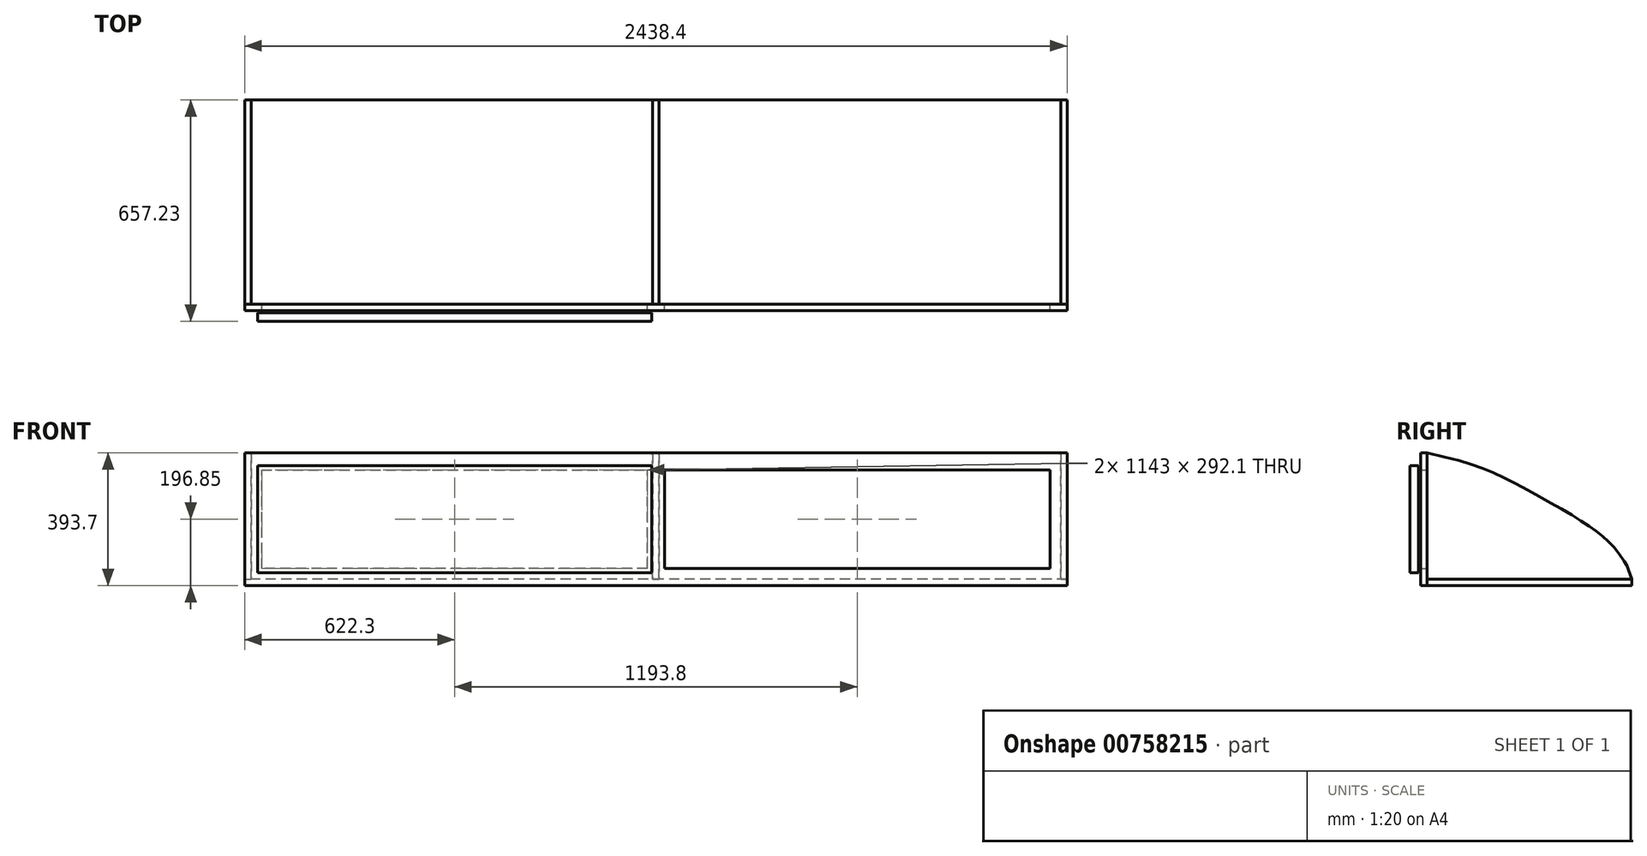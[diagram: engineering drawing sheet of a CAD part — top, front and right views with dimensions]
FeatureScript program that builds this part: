
annotation { "Feature Type Name" : "Feature", "Feature Type Description" : "" }
export const myFeature = defineFeature(function(context is Context, id is Id, definition is map)
    precondition{}
    {
        {
            var Q0;
            Q0=qCreatedBy(makeId("Front.planeOp"),FACE);
            var sketch = newSketch(context, id + "F0", { "sketchPlane" : qUnion([Q0])});
            skLineSegment(sketch, "E0", {"start": v(-1150.95, 0) * mm, "end": v(1287.45, 0) * mm});
            skLineSegment(sketch, "E1", {"start": v(1287.45, 0) * mm, "end": v(1287.45, 50.8) * mm});
            skLineSegment(sketch, "E2", {"start": v(1287.45, 50.8) * mm, "end": v(-1150.95, 50.8) * mm});
            skLineSegment(sketch, "E3", {"start": v(-1150.95, 50.8) * mm, "end": v(-1150.95, 0) * mm});
            skLineSegment(sketch, "E4.bottom", {"start": v(-1150.95, 50.8) * mm, "end": v(-1100.15, 50.8) * mm});
            skLineSegment(sketch, "E4.top", {"start": v(-1150.95, 342.9) * mm, "end": v(-1100.15, 342.9) * mm});
            skLineSegment(sketch, "E4.left", {"start": v(-1150.95, 50.8) * mm, "end": v(-1150.95, 342.9) * mm});
            skLineSegment(sketch, "E4.right", {"start": v(-1100.15, 50.8) * mm, "end": v(-1100.15, 342.9) * mm});
            skLineSegment(sketch, "E5.bottom", {"start": v(1287.45, 50.8) * mm, "end": v(1236.65, 50.8) * mm});
            skLineSegment(sketch, "E5.top", {"start": v(1287.45, 342.9) * mm, "end": v(1236.65, 342.9) * mm});
            skLineSegment(sketch, "E5.left", {"start": v(1287.45, 50.8) * mm, "end": v(1287.45, 342.9) * mm});
            skLineSegment(sketch, "E5.right", {"start": v(1236.65, 50.8) * mm, "end": v(1236.65, 342.9) * mm});
            skLineSegment(sketch, "E6.left", {"start": v(93.65, 50.8) * mm, "end": v(93.65, 342.9) * mm});
            skLineSegment(sketch, "E6.right", {"start": v(42.85, 50.8) * mm, "end": v(42.85, 342.9) * mm});
            skLineSegment(sketch, "E7.bottom", {"start": v(-1150.95, 342.9) * mm, "end": v(1287.45, 342.9) * mm});
            skLineSegment(sketch, "E7.top", {"start": v(-1150.95, 393.7) * mm, "end": v(1287.45, 393.7) * mm});
            skLineSegment(sketch, "E7.left", {"start": v(-1150.95, 342.9) * mm, "end": v(-1150.95, 393.7) * mm});
            skLineSegment(sketch, "E7.right", {"start": v(1287.45, 342.9) * mm, "end": v(1287.45, 393.7) * mm});
            skLineSegment(sketch, "E8", {"start": v(68.25, 342.9) * mm, "end": v(68.25, 50.8) * mm, "construction": true});
            skLineSegment(sketch, "E9", {"start": v(42.85, 342.9) * mm, "end": v(93.65, 342.9) * mm});
            skLineSegment(sketch, "E10", {"start": v(42.85, 50.8) * mm, "end": v(93.65, 50.8) * mm});
            skSolve(sketch);
        }
        {
            var Q0;
            {var subQ1=sQuery(id+"F0.wireOp",EDGE,"E4.top");Q0=makeQuery(id+"F0.imprint","IMPRINT",FACE,{"disambiguationData":[TD([[makeQuery(id+"F0.imprint","IMPRINT",EDGE,{"derivedFrom":subQ1}),1.0]])]});}
            var Q1;
            Q1=makeQuery(id+"F0.imprint","IMPRINT",FACE,{"disambiguationData":[TD([[makeQuery(id+"F0.imprint","IMPRINT",EDGE,{"derivedFrom":sQuery(id+"F0.wireOp",EDGE,"E4.top")}),-1.0]])]});
            var Q2;
            Q2=makeQuery(id+"F0.imprint","IMPRINT",FACE,{"disambiguationData":[TD([[makeQuery(id+"F0.imprint","IMPRINT",EDGE,{"derivedFrom":sQuery(id+"F0.wireOp",EDGE,"E0")}),1.0]])]});
            var Q3;
            {var subQ0=sQuery(id+"F0.wireOp",EDGE,"E6.left");Q3=makeQuery(id+"F0.imprint","IMPRINT",FACE,{"disambiguationData":[TD([[makeQuery(id+"F0.imprint","IMPRINT",EDGE,{"derivedFrom":subQ0}),1.0]])]});}
            var Q4;
            Q4=makeQuery(id+"F0.imprint","IMPRINT",FACE,{"disambiguationData":[TD([[makeQuery(id+"F0.imprint","IMPRINT",EDGE,{"derivedFrom":sQuery(id+"F0.wireOp",EDGE,"E5.top")}),1.0]])]});
            extrude(context, id + "F1", {"entities" : qUnion([Q0, Q1, Q2, Q3, Q4]), "depth" : 19.05 * mm, "offsetDistance" : 25.4 * mm});
        }
        {
            var Q0;
            Q0=makeQuery(id+"F1.opExtrude","CAP_FACE",FACE,{"disambiguationData":[OSD([sQuery(id+"F0.wireOp",EDGE,"E0"),sQuery(id+"F0.wireOp",EDGE,"E1"),sQuery(id+"F0.wireOp",EDGE,"E2"),sQuery(id+"F0.wireOp",EDGE,"E3"),sQuery(id+"F0.wireOp",EDGE,"E4.left"),sQuery(id+"F0.wireOp",EDGE,"E4.right"),sQuery(id+"F0.wireOp",EDGE,"E5.left"),sQuery(id+"F0.wireOp",EDGE,"E5.right"),sQuery(id+"F0.wireOp",EDGE,"E6.left"),sQuery(id+"F0.wireOp",EDGE,"E6.right"),sQuery(id+"F0.wireOp",EDGE,"E7.bottom"),sQuery(id+"F0.wireOp",EDGE,"E7.top"),sQuery(id+"F0.wireOp",EDGE,"E7.left"),sQuery(id+"F0.wireOp",EDGE,"E7.right")])],"isStart":true});
            var sketch = newSketch(context, id + "F2", { "sketchPlane" : qUnion([Q0])});
            skLineSegment(sketch, "E11.bottom", {"start": v(-1287.45, 0) * mm, "end": v(1150.95, 0) * mm});
            skLineSegment(sketch, "E11.top", {"start": v(-1287.45, 19.05) * mm, "end": v(1150.95, 19.05) * mm});
            skLineSegment(sketch, "E11.left", {"start": v(-1287.45, 0) * mm, "end": v(-1287.45, 19.05) * mm});
            skLineSegment(sketch, "E11.right", {"start": v(1150.95, 0) * mm, "end": v(1150.95, 19.05) * mm});
            skSolve(sketch);
        }
        {
            var Q0;
            Q0=makeQuery(id+"F2.imprint","IMPRINT",FACE,{"disambiguationData":[TD([[makeQuery(id+"F2.imprint","IMPRINT",EDGE,{"derivedFrom":sQuery(id+"F2.wireOp",EDGE,"E11.bottom")}),-1.0]])]});
            extrude(context, id + "F3", {"entities" : qUnion([Q0]), "depth" : 606.42 * mm, "offsetDistance" : 25.4 * mm});
        }
        {
            var Q0;
            Q0=makeQuery(id+"F1.opExtrude","SWEPT_FACE",FACE,{"disambiguationData":[OSD([sQuery(id+"F0.wireOp",EDGE,"E1"),sQuery(id+"F0.wireOp",EDGE,"E5.left"),sQuery(id+"F0.wireOp",EDGE,"E7.right")])]});
            cPlane(context, id + "F4", {"entities" : qUnion([Q0]), "cplaneType" : CPlaneType.OFFSET, "offset" : 0 * mm, "width" : 152.4 * mm, "height" : 152.4 * mm});
        }
        {
            var Q0;
            Q0=qCreatedBy(id+"F4.planeOp",FACE);
            var sketch = newSketch(context, id + "F5", { "sketchPlane" : qUnion([Q0])});
            skLineSegment(sketch, "E12.0", {"start": v(0, 19.05) * mm, "end": v(0, 393.7) * mm});
            skLineSegment(sketch, "E13.0", {"start": v(606.43, 19.05) * mm, "end": v(0, 19.05) * mm});
            skLineSegment(sketch, "E14.0", {"start": v(-19.05, 0) * mm, "end": v(0, 0) * mm});
            skFitSpline(sketch, "E15", {"points": [v(0, 393.7) * mm, v(180.53, 341.58) * mm, v(321.82, 269.99) * mm, v(447.9, 197.13) * mm, v(513.79, 150.87) * mm, v(558.77, 107.16) * mm, v(591.08, 60.9) * mm, v(606.43, 19.05) * mm], "startDerivative": vector(1328.19, -310.67) * mm, "endDerivative": vector(351.9, -1041.55) * mm});
            skSolve(sketch);
        }
        {
            var Q0;
            Q0=makeQuery(id+"F5.imprint","IMPRINT",FACE,{"disambiguationData":[TD([[makeQuery(id+"F5.imprint","IMPRINT",EDGE,{"derivedFrom":sQuery(id+"F5.wireOp",EDGE,"E12.0")}),-1.0]])]});
            extrude(context, id + "F6", {"entities" : qUnion([Q0]), "oppositeDirection" : true, "depth" : 19.05 * mm, "offsetDistance" : 25.4 * mm});
        }
        {
            var Q0;
            Q0=makeQuery(id+"F6.opExtrude","SWEPT_BODY",BODY,{"disambiguationData":[OSD([sQuery(id+"F5.wireOp",EDGE,"E12.0"),sQuery(id+"F5.wireOp",EDGE,"E13.0"),sQuery(id+"F5.wireOp",EDGE,"E15")])]});
            transform(context, id + "F7", {"entities" : qUnion([Q0]), "transformType" : TransformType.TRANSLATION_3D, "dx" : -2419.35 * mm, "dy" : 0 * mm, "dz" : 0 * mm, "makeCopy" : true});
        }
        {
            var Q0;
            Q0=makeQuery(id+"F6.opExtrude","SWEPT_BODY",BODY,{"disambiguationData":[OSD([sQuery(id+"F5.wireOp",EDGE,"E12.0"),sQuery(id+"F5.wireOp",EDGE,"E13.0"),sQuery(id+"F5.wireOp",EDGE,"E15")])]});
            transform(context, id + "F8", {"entities" : qUnion([Q0]), "transformType" : TransformType.TRANSLATION_3D, "dx" : -1209.67 * mm, "dy" : 0 * mm, "dz" : 0 * mm, "makeCopy" : true});
        }
        {
            var Q0;
            Q0=makeQuery(id+"F1.opExtrude","CAP_FACE",FACE,{"disambiguationData":[OSD([sQuery(id+"F0.wireOp",EDGE,"E0"),sQuery(id+"F0.wireOp",EDGE,"E1"),sQuery(id+"F0.wireOp",EDGE,"E2"),sQuery(id+"F0.wireOp",EDGE,"E3"),sQuery(id+"F0.wireOp",EDGE,"E4.left"),sQuery(id+"F0.wireOp",EDGE,"E4.right"),sQuery(id+"F0.wireOp",EDGE,"E5.left"),sQuery(id+"F0.wireOp",EDGE,"E5.right"),sQuery(id+"F0.wireOp",EDGE,"E6.left"),sQuery(id+"F0.wireOp",EDGE,"E6.right"),sQuery(id+"F0.wireOp",EDGE,"E7.bottom"),sQuery(id+"F0.wireOp",EDGE,"E7.top"),sQuery(id+"F0.wireOp",EDGE,"E7.left"),sQuery(id+"F0.wireOp",EDGE,"E7.right")])],"isStart":false});
            cPlane(context, id + "F9", {"entities" : qUnion([Q0]), "cplaneType" : CPlaneType.OFFSET, "offset" : 6.35 * mm, "width" : 152.4 * mm, "height" : 152.4 * mm});
        }
        {
            var Q0;
            Q0=qCreatedBy(id+"F9.planeOp",FACE);
            var sketch = newSketch(context, id + "F10", { "sketchPlane" : qUnion([Q0])});
            skLineSegment(sketch, "E16.0", {"start": v(-1112.85, 355.6) * mm, "end": v(55.55, 355.6) * mm});
            skLineSegment(sketch, "E17.0", {"start": v(-1112.85, 38.1) * mm, "end": v(-1112.85, 355.6) * mm});
            skLineSegment(sketch, "E18.0", {"start": v(55.55, 38.1) * mm, "end": v(-1112.85, 38.1) * mm});
            skLineSegment(sketch, "E19.0", {"start": v(55.55, 38.1) * mm, "end": v(55.55, 355.6) * mm});
            skLineSegment(sketch, "E20", {"start": v(-528.65, 50.8) * mm, "end": v(-528.65, 342.9) * mm, "construction": true});
            skLineSegment(sketch, "E21", {"start": v(42.85, 196.85) * mm, "end": v(-1100.15, 196.85) * mm, "construction": true});
            skLineSegment(sketch, "E22", {"start": v(-1112.85, 355.6) * mm, "end": v(55.55, 38.1) * mm, "construction": true});
            skLineSegment(sketch, "E23", {"start": v(55.55, 355.6) * mm, "end": v(-1112.85, 38.1) * mm, "construction": true});
            skPoint(sketch, "E24", {"position": v(-528.65, 196.85) * mm});
            skSolve(sketch);
        }
        {
            var Q0;
            Q0 = qSketchRegion(id + "F10", true);
            extrude(context, id + "F11", {"entities" : qUnion([Q0]), "depth" : 25.4 * mm, "offsetDistance" : 25.4 * mm});
        }
    });
